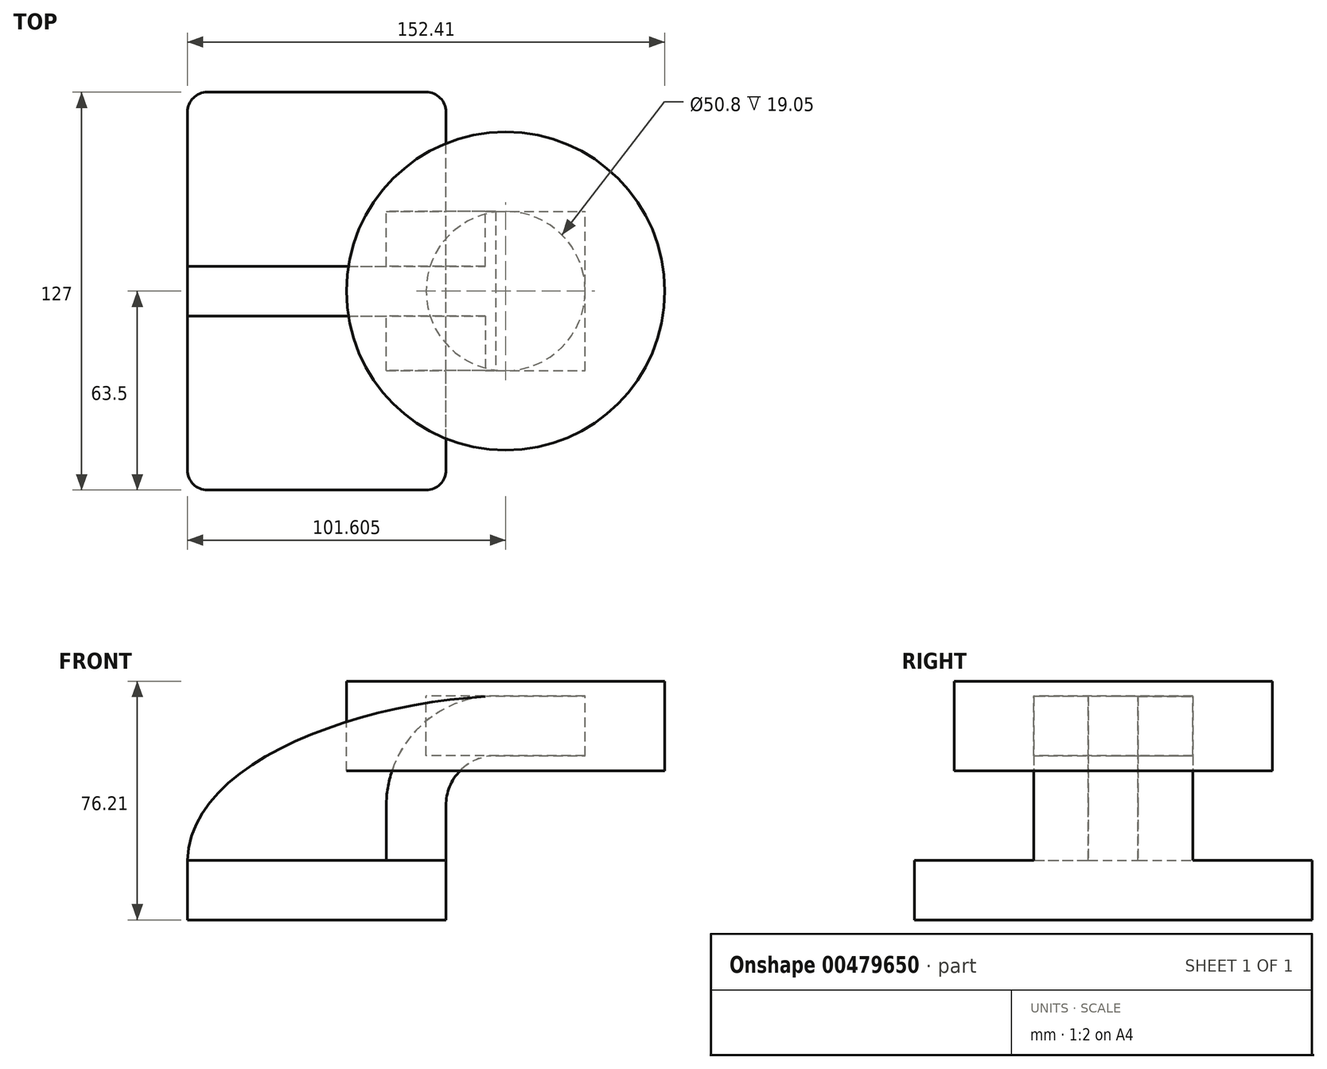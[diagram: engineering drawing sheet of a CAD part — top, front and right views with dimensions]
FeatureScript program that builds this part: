
annotation { "Feature Type Name" : "Feature", "Feature Type Description" : "" }
export const myFeature = defineFeature(function(context is Context, id is Id, definition is map)
    precondition{}
    {
        {
            var Q0;
            Q0=qCreatedBy(makeId("Front.planeOp"),FACE);
            var sketch = newSketch(context, id + "F0", { "sketchPlane" : qUnion([Q0])});
            skLineSegment(sketch, "E0.bottom", {"start": v(-41.28, 9.53) * mm, "end": v(41.27, 9.53) * mm});
            skLineSegment(sketch, "E0.top", {"start": v(-41.28, -9.52) * mm, "end": v(41.28, -9.52) * mm});
            skLineSegment(sketch, "E0.left", {"start": v(-41.28, 9.53) * mm, "end": v(-41.27, -9.52) * mm});
            skLineSegment(sketch, "E0.right", {"start": v(41.28, 9.53) * mm, "end": v(41.28, -9.52) * mm});
            skPoint(sketch, "E0.middle", {"position": v(0, 0) * mm});
            skLineSegment(sketch, "E1.bottom", {"start": v(60.33, 66.68) * mm, "end": v(111.12, 66.68) * mm});
            skLineSegment(sketch, "E1.top", {"start": v(60.33, 38.1) * mm, "end": v(111.12, 38.1) * mm});
            skLineSegment(sketch, "E1.left", {"start": v(60.33, 66.68) * mm, "end": v(60.33, 38.1) * mm});
            skLineSegment(sketch, "E1.right", {"start": v(111.12, 66.68) * mm, "end": v(111.12, 38.1) * mm});
            skPoint(sketch, "E1.middle", {"position": v(85.72, 52.39) * mm});
            skLineSegment(sketch, "E2", {"start": v(41.27, 27) * mm, "end": v(41.27, 9.53) * mm});
            skArc(sketch, "E3", {"start": v(41.27, 27) * mm, "mid": v(45.92, 38.23) * mm, "end": v(57.15, 42.88) * mm});
            skLineSegment(sketch, "E4", {"start": v(57.15, 42.88) * mm, "end": v(85.72, 42.88) * mm});
            skLineSegment(sketch, "E5.0", {"start": v(22.23, 27) * mm, "end": v(22.23, 9.53) * mm});
            skArc(sketch, "E5.1", {"start": v(22.22, 27) * mm, "mid": v(32.45, 51.7) * mm, "end": v(57.15, 61.93) * mm});
            skLineSegment(sketch, "E5.2", {"start": v(57.15, 61.93) * mm, "end": v(85.72, 61.93) * mm});
            skLineSegment(sketch, "E6", {"start": v(85.72, 42.88) * mm, "end": v(85.72, 61.93) * mm});
            skFitSpline(sketch, "E7", {"points": [v(-41.27, 9.53) * mm, v(57.15, 61.93) * mm], "startDerivative": vector(1.85, 94.7) * mm, "endDerivative": vector(128.85, 4.9) * mm});
            skSolve(sketch);
        }
        {
            var Q0;
            Q0=qCreatedBy(makeId("Front.planeOp"),FACE);
            var sketch = newSketch(context, id + "F1", { "sketchPlane" : qUnion([Q0])});
            skSolve(sketch);
        }
        {
            var Q0;
            Q0=makeQuery(id+"F0.imprint","IMPRINT",FACE,{"disambiguationData":[TD([[makeQuery(id+"F0.imprint","IMPRINT",EDGE,{"derivedFrom":sQuery(id+"F0.wireOp",EDGE,"E0.top")}),1.0]])]});
            var Q1;
            Q1 = qSketchRegion(id + "F1", true);
            extrude(context, id + "F2", {"entities" : qUnion([Q0, Q1]), "endBound" : BoundingType.SYMMETRIC, "depth" : 127 * mm});
        }
        {
            var Q0;
            Q0 = qSketchRegion(id + "F1", true);
            var Q1;
            {var subQ1=sQuery(id+"F0.wireOp",EDGE,"E2");Q1=makeQuery(id+"F0.imprint","IMPRINT",FACE,{"disambiguationData":[TD([[makeQuery(id+"F0.imprint","IMPRINT",EDGE,{"derivedFrom":subQ1}),-1.0]])]});}
            var Q2;
            {var subQ5=sQuery(id+"F0.wireOp",EDGE,"E6");Q2=makeQuery(id+"F0.imprint","IMPRINT",FACE,{"disambiguationData":[TD([[makeQuery(id+"F0.imprint","IMPRINT",EDGE,{"derivedFrom":subQ5}),1.0]])]});}
            extrude(context, id + "F3", {"entities" : qUnion([Q0, Q1, Q2]), "operationType" : NewBodyOperationType.ADD, "endBound" : BoundingType.SYMMETRIC, "depth" : 50.8 * mm});
        }
        {
            var Q0;
            {var subQ3=sQuery(id+"F0.wireOp",EDGE,"E5.0");Q0=makeQuery(id+"F0.imprint","IMPRINT",FACE,{"disambiguationData":[TD([[makeQuery(id+"F0.imprint","IMPRINT",EDGE,{"derivedFrom":subQ3}),-1.0]])]});}
            extrude(context, id + "F4", {"entities" : qUnion([Q0]), "operationType" : NewBodyOperationType.ADD, "endBound" : BoundingType.SYMMETRIC, "depth" : 15.88 * mm});
        }
        {
            var Q0;
            {var subQ5=sQuery(id+"F0.wireOp",EDGE,"E1.bottom");Q0=makeQuery(id+"F0.imprint","IMPRINT",FACE,{"disambiguationData":[TD([[makeQuery(id+"F0.imprint","IMPRINT",EDGE,{"derivedFrom":subQ5}),-1.0]])]});}
            var Q1;
            Q1=sQuery(id+"F0.wireOp",EDGE,"E1.left");
            revolve(context, id + "F5", {"entities" : qUnion([Q0]), "axis" : qUnion([Q1]), "revolveType" : RevolveType.FULL});
        }
        {
            var Q0;
            Q0=makeQuery(id+"F2.opExtrude","CAP_EDGE",EDGE,{"disambiguationData":[OSD([sQuery(id+"F0.wireOp",EDGE,"E0.right")])],"isStart":false});
            var Q1;
            Q1=makeQuery(id+"F2.opExtrude","CAP_EDGE",EDGE,{"disambiguationData":[OSD([sQuery(id+"F0.wireOp",EDGE,"E0.left")])],"isStart":false});
            var Q2;
            Q2=makeQuery(id+"F2.opExtrude","CAP_EDGE",EDGE,{"disambiguationData":[OSD([sQuery(id+"F0.wireOp",EDGE,"E0.right")])],"isStart":true});
            var Q3;
            Q3=makeQuery(id+"F2.opExtrude","CAP_EDGE",EDGE,{"disambiguationData":[OSD([sQuery(id+"F0.wireOp",EDGE,"E0.left")])],"isStart":true});
            fillet(context, id + "F6", {"entities" : qUnion([Q0, Q1, Q2, Q3]), "radius" : 6.35 * mm, "tangentPropagation" : true, "allowEdgeOverflow" : false});
        }
    });
